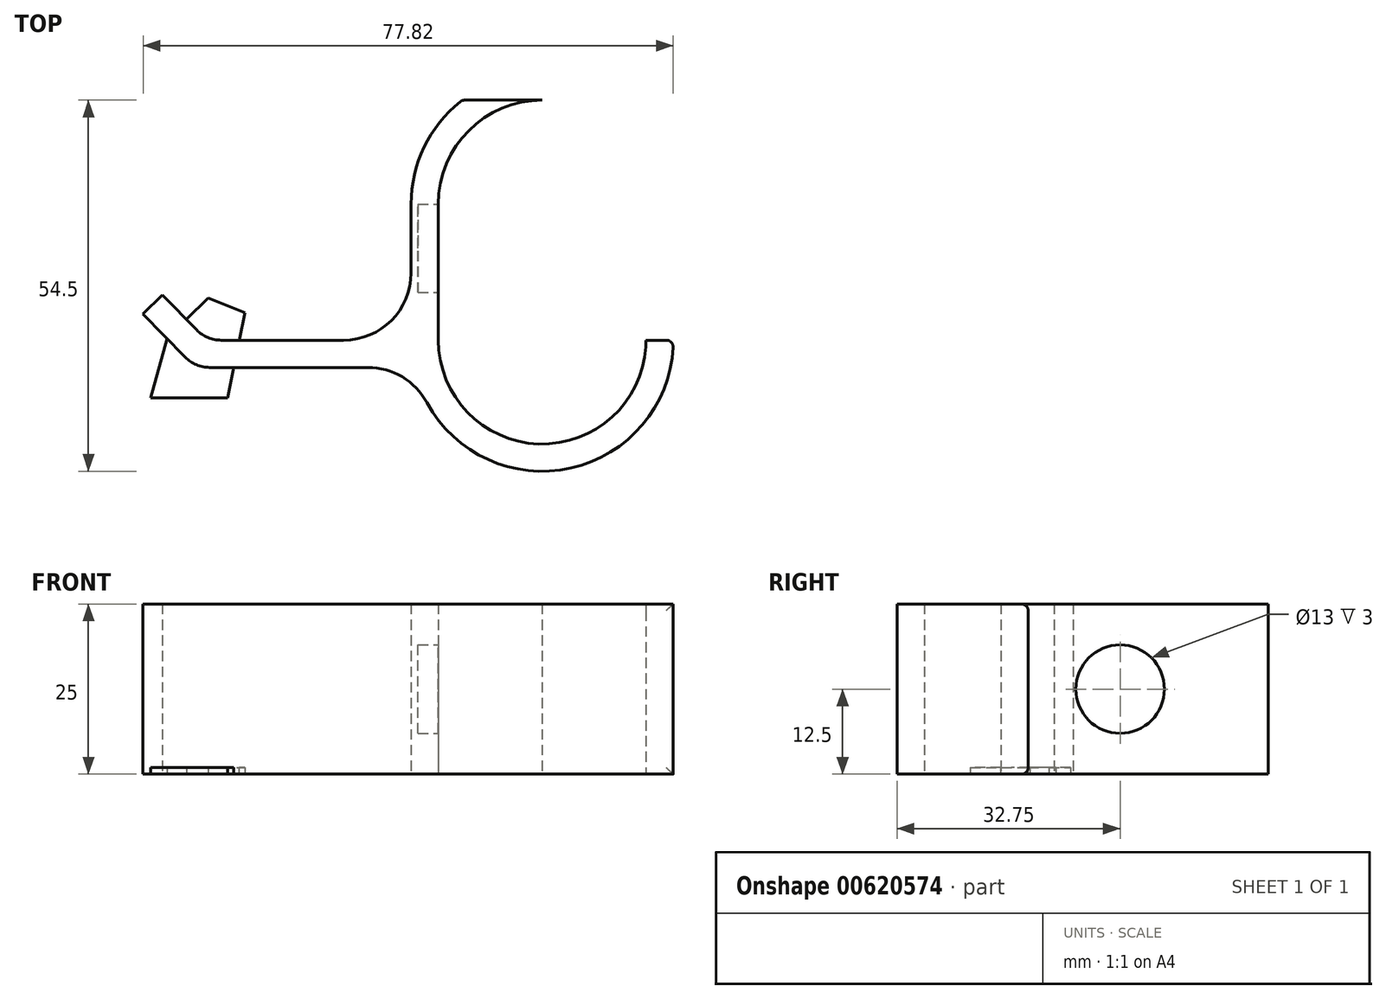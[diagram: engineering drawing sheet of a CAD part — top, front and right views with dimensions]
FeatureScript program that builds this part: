
annotation { "Feature Type Name" : "Feature", "Feature Type Description" : "" }
export const myFeature = defineFeature(function(context is Context, id is Id, definition is map)
    precondition{}
    {
        {
            var Q0;
            Q0=qCreatedBy(makeId("Top.planeOp"),FACE);
            var sketch = newSketch(context, id + "F0", { "sketchPlane" : qUnion([Q0])});
            skLineSegment(sketch, "E0", {"start": v(0, 0) * mm, "end": v(0, 20) * mm});
            skArc(sketch, "E1", {"start": v(15.25, 35.25) * mm, "mid": v(4.47, 30.78) * mm, "end": v(0, 20) * mm});
            skArc(sketch, "E2", {"start": v(0, 0) * mm, "mid": v(15.25, -15.25) * mm, "end": v(30.5, 0) * mm});
            skArc(sketch, "E3.0", {"start": v(-3.58, -4) * mm, "mid": v(17.26, -19.14) * mm, "end": v(34.5, 0) * mm});
            skLineSegment(sketch, "E3.1", {"start": v(-4, 0) * mm, "end": v(-4, 20) * mm});
            skArc(sketch, "E3.2", {"start": v(3.5, 35.25) * mm, "mid": v(-2.02, 28.5) * mm, "end": v(-4, 20) * mm});
            skLineSegment(sketch, "E4", {"start": v(15.25, 35.25) * mm, "end": v(3.5, 35.25) * mm});
            skLineSegment(sketch, "E5", {"start": v(30.5, 0) * mm, "end": v(34.5, 0) * mm});
            skPoint(sketch, "E6.orphan", {"position": v(30.5, 20) * mm});
            skLineSegment(sketch, "E7", {"start": v(-4, 0) * mm, "end": v(-34, 0) * mm});
            skLineSegment(sketch, "E8", {"start": v(-34, 0) * mm, "end": v(-40.5, 6.62) * mm});
            skLineSegment(sketch, "E9.0", {"start": v(-35.68, -4) * mm, "end": v(-43.35, 3.82) * mm});
            skLineSegment(sketch, "E9.1", {"start": v(-3.58, -4) * mm, "end": v(-35.68, -4) * mm});
            skLineSegment(sketch, "E10", {"start": v(-40.5, 6.62) * mm, "end": v(-43.35, 3.82) * mm});
            skSolve(sketch);
        }
        {
            var Q0;
            Q0=makeQuery(id+"F0.imprint","IMPRINT",FACE,{"disambiguationData":[TD([[makeQuery(id+"F0.imprint","IMPRINT",EDGE,{"derivedFrom":sQuery(id+"F0.wireOp",EDGE,"E0")}),1.0]])]});
            extrude(context, id + "F1", {"entities" : qUnion([Q0]), "depth" : 25 * mm, "offsetDistance" : 25 * mm});
        }
        {
            var Q0;
            Q0=makeQuery(id+"F1.opExtrude","SWEPT_EDGE",EDGE,{"disambiguationData":[OSD([sQuery(id+"F0.wireOp",EDGE,"E9.0"),sQuery(id+"F0.wireOp",EDGE,"E9.1")])]});
            var Q1;
            Q1=makeQuery(id+"F1.opExtrude","SWEPT_EDGE",EDGE,{"disambiguationData":[OSD([sQuery(id+"F0.wireOp",EDGE,"E7"),sQuery(id+"F0.wireOp",EDGE,"E8")])]});
            fillet(context, id + "F2", {"entities" : qUnion([Q0, Q1]), "radius" : 5 * mm, "tangentPropagation" : true, "allowEdgeOverflow" : false});
        }
        {
            var Q0;
            Q0=makeQuery(id+"F1.opExtrude","SWEPT_EDGE",EDGE,{"disambiguationData":[OSD([sQuery(id+"F0.wireOp",EDGE,"E3.0"),sQuery(id+"F0.wireOp",EDGE,"E9.1")])]});
            var Q1;
            Q1=makeQuery(id+"F1.opExtrude","SWEPT_EDGE",EDGE,{"disambiguationData":[OSD([sQuery(id+"F0.wireOp",EDGE,"E3.1"),sQuery(id+"F0.wireOp",EDGE,"E7")])]});
            fillet(context, id + "F3", {"entities" : qUnion([Q0, Q1]), "radius" : 9.9 * mm, "tangentPropagation" : true, "allowEdgeOverflow" : false});
        }
        {
            var Q0;
            Q0=makeQuery(id+"F1.opExtrude","SWEPT_EDGE",EDGE,{"disambiguationData":[OSD([sQuery(id+"F0.wireOp",EDGE,"E3.0"),sQuery(id+"F0.wireOp",EDGE,"E5")])]});
            var Q1;
            Q1=makeQuery(id+"F1.opExtrude","CAP_EDGE",EDGE,{"disambiguationData":[OSD([sQuery(id+"F0.wireOp",EDGE,"E5")])],"isStart":false});
            var Q2;
            Q2=makeQuery(id+"F1.opExtrude","CAP_EDGE",EDGE,{"disambiguationData":[OSD([sQuery(id+"F0.wireOp",EDGE,"E5")])],"isStart":true});
            var Q3;
            Q3=makeQuery(id+"F1.opExtrude","SWEPT_EDGE",EDGE,{"disambiguationData":[OSD([sQuery(id+"F0.wireOp",EDGE,"E3.2"),sQuery(id+"F0.wireOp",EDGE,"E4")])]});
            fillet(context, id + "F4", {"entities" : qUnion([Q0, Q1, Q2, Q3]), "radius" : 1 * mm, "tangentPropagation" : true, "allowEdgeOverflow" : false});
        }
        {
            var Q0;
            Q0=makeQuery(id+"F1.opExtrude","SWEPT_FACE",FACE,{"disambiguationData":[OSD([sQuery(id+"F0.wireOp",EDGE,"E0")])]});
            var sketch = newSketch(context, id + "F5", { "sketchPlane" : qUnion([Q0])});
            skLineSegment(sketch, "E11", {"start": v(20, 12.5) * mm, "end": v(13.5, 12.5) * mm});
            skPoint(sketch, "E11.endSnap0", {"position": v(20, 12.5) * mm});
            skCircle(sketch, "E12", {"center": v(13.5, 12.5) * mm, "radius": 6.5 * mm});
            skSolve(sketch);
        }
        {
            var Q0;
            Q0 = qSketchRegion(id + "F5", true);
            extrude(context, id + "F6", {"entities" : qUnion([Q0]), "operationType" : NewBodyOperationType.REMOVE, "oppositeDirection" : true, "depth" : 3 * mm, "offsetDistance" : 25 * mm});
        }
        {
            var Q0;
            Q0=makeQuery(id+"F1.opExtrude","CAP_FACE",FACE,{"disambiguationData":[OSD([sQuery(id+"F0.wireOp",EDGE,"E0"),sQuery(id+"F0.wireOp",EDGE,"E1"),sQuery(id+"F0.wireOp",EDGE,"E2"),sQuery(id+"F0.wireOp",EDGE,"E3.0"),sQuery(id+"F0.wireOp",EDGE,"E3.1"),sQuery(id+"F0.wireOp",EDGE,"E3.2"),sQuery(id+"F0.wireOp",EDGE,"E4"),sQuery(id+"F0.wireOp",EDGE,"E5"),sQuery(id+"F0.wireOp",EDGE,"E7"),sQuery(id+"F0.wireOp",EDGE,"E8"),sQuery(id+"F0.wireOp",EDGE,"E9.0"),sQuery(id+"F0.wireOp",EDGE,"E9.1"),sQuery(id+"F0.wireOp",EDGE,"E10")])],"isStart":true});
            var sketch = newSketch(context, id + "F7", { "sketchPlane" : qUnion([Q0])});
            skLineSegment(sketch, "E13", {"start": v(-39.85, -0.25) * mm, "end": v(-33.8, -6.2) * mm});
            skLineSegment(sketch, "E14", {"start": v(-33.8, -6.2) * mm, "end": v(-28.43, -4.06) * mm});
            skLineSegment(sketch, "E15", {"start": v(-28.43, -4.06) * mm, "end": v(-30.91, 8.49) * mm});
            skLineSegment(sketch, "E16", {"start": v(-30.91, 8.49) * mm, "end": v(-42.23, 8.49) * mm});
            skLineSegment(sketch, "E17", {"start": v(-42.23, 8.49) * mm, "end": v(-39.85, -0.25) * mm});
            skSolve(sketch);
        }
        {
            var Q0;
            Q0 = qSketchRegion(id + "F7", true);
            extrude(context, id + "F8", {"entities" : qUnion([Q0]), "operationType" : NewBodyOperationType.ADD, "oppositeDirection" : true, "depth" : 1 * mm, "offsetDistance" : 25 * mm});
        }
    });
